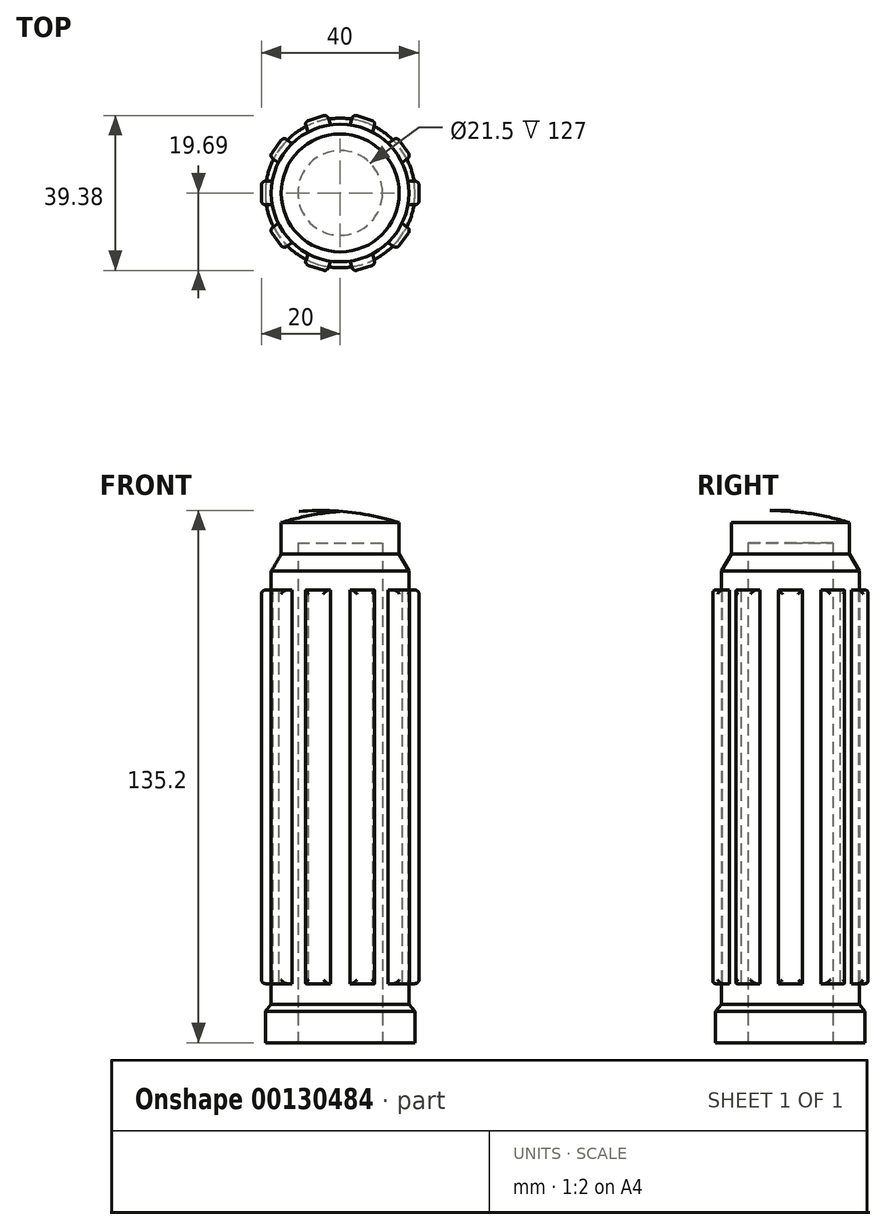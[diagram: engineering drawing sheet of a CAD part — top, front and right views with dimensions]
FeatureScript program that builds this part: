
annotation { "Feature Type Name" : "Feature", "Feature Type Description" : "" }
export const myFeature = defineFeature(function(context is Context, id is Id, definition is map)
    precondition{}
    {
        {
            var Q0;
            Q0=qCreatedBy(makeId("Front.planeOp"),FACE);
            var sketch = newSketch(context, id + "F0", { "sketchPlane" : qUnion([Q0])});
            skLineSegment(sketch, "E0", {"start": v(0, 135) * mm, "end": v(0, 127) * mm});
            skLineSegment(sketch, "E1", {"start": v(0, 127) * mm, "end": v(10.75, 127) * mm});
            skLineSegment(sketch, "E2", {"start": v(10.75, 127) * mm, "end": v(10.75, 0) * mm});
            skLineSegment(sketch, "E3", {"start": v(10.75, 0) * mm, "end": v(19, 0) * mm});
            skLineSegment(sketch, "E4", {"start": v(19, 0) * mm, "end": v(19, 8) * mm});
            skLineSegment(sketch, "E5", {"start": v(19, 8) * mm, "end": v(17.5, 9.79) * mm});
            skLineSegment(sketch, "E6", {"start": v(17.5, 9.79) * mm, "end": v(17.5, 119.79) * mm});
            skLineSegment(sketch, "E7", {"start": v(15, 124.12) * mm, "end": v(15, 132.12) * mm});
            skArc(sketch, "E8", {"start": v(15, 132.12) * mm, "mid": v(7.58, 133.98) * mm, "end": v(0, 135) * mm});
            skLineSegment(sketch, "E9", {"start": v(17.5, 119.79) * mm, "end": v(15, 124.12) * mm});
            skLineSegment(sketch, "E10", {"start": v(0, 0) * mm, "end": v(0, 165.13) * mm, "construction": true});
            skSolve(sketch);
        }
        {
            var Q0;
            Q0=makeQuery(id+"F0.imprint","IMPRINT",FACE,{"disambiguationData":[TD([[makeQuery(id+"F0.imprint","IMPRINT",EDGE,{"derivedFrom":sQuery(id+"F0.wireOp",EDGE,"E0")}),1.0]])]});
            var Q1;
            Q1=sQuery(id+"F0.wireOp",EDGE,"E10");
            revolve(context, id + "F1", {"entities" : qUnion([Q0]), "axis" : qUnion([Q1]), "revolveType" : RevolveType.FULL});
        }
        {
            var Q0;
            Q0=qCreatedBy(makeId("Right.planeOp"),FACE);
            cPlane(context, id + "F2", {"entities" : qUnion([Q0]), "cplaneType" : CPlaneType.OFFSET, "offset" : 20 * mm, "width" : 150 * mm, "height" : 150 * mm});
        }
        {
            var Q0;
            Q0=qCreatedBy(id+"F2.planeOp",FACE);
            var sketch = newSketch(context, id + "F3", { "sketchPlane" : qUnion([Q0])});
            skLineSegment(sketch, "E11.bottom", {"start": v(-3, 115) * mm, "end": v(3, 115) * mm});
            skLineSegment(sketch, "E11.top", {"start": v(-3, 15) * mm, "end": v(3, 15) * mm});
            skLineSegment(sketch, "E11.left", {"start": v(-3, 115) * mm, "end": v(-3, 15) * mm});
            skLineSegment(sketch, "E11.right", {"start": v(3, 115) * mm, "end": v(3, 15) * mm});
            skSolve(sketch);
        }
        {
            var Q0;
            Q0=makeQuery(id+"F3.imprint","IMPRINT",FACE,{"disambiguationData":[TD([[makeQuery(id+"F3.imprint","IMPRINT",EDGE,{"derivedFrom":sQuery(id+"F3.wireOp",EDGE,"E11.bottom")}),-1.0]])]});
            var Q1;
            Q1=makeQuery(id+"F1.opRevolve","SWEPT_FACE",FACE,{"disambiguationData":[OSD([sQuery(id+"F0.wireOp",EDGE,"E6")])]});
            extrude(context, id + "F4", {"entities" : qUnion([Q0]), "endBound" : BoundingType.UP_TO_SURFACE, "oppositeDirection" : true, "endBoundEntityFace" : qUnion([Q1]), "depth" : 25 * mm});
        }
        {
            var Q0;
            Q0=makeQuery(id+"F4.opExtrude","CAP_EDGE",EDGE,{"disambiguationData":[OSD([sQuery(id+"F3.wireOp",EDGE,"E11.right")])],"isStart":true});
            var Q1;
            Q1=makeQuery(id+"F4.opExtrude","CAP_EDGE",EDGE,{"disambiguationData":[OSD([sQuery(id+"F3.wireOp",EDGE,"E11.bottom")])],"isStart":true});
            var Q2;
            Q2=makeQuery(id+"F4.opExtrude","CAP_EDGE",EDGE,{"disambiguationData":[OSD([sQuery(id+"F3.wireOp",EDGE,"E11.top")])],"isStart":true});
            var Q3;
            Q3=makeQuery(id+"F4.opExtrude","CAP_EDGE",EDGE,{"disambiguationData":[OSD([sQuery(id+"F3.wireOp",EDGE,"E11.left")])],"isStart":true});
            fillet(context, id + "F5", {"entities" : qUnion([Q0, Q1, Q2, Q3]), "radius" : 1 * mm, "tangentPropagation" : true, "allowEdgeOverflow" : false});
        }
        {
            var Q0;
            Q0=makeQuery(id+"F4.opExtrude","SWEPT_BODY",BODY,{"disambiguationData":[OSD([sQuery(id+"F3.wireOp",EDGE,"E11.bottom"),sQuery(id+"F3.wireOp",EDGE,"E11.top"),sQuery(id+"F3.wireOp",EDGE,"E11.left"),sQuery(id+"F3.wireOp",EDGE,"E11.right")])]});
            var Q1;
            Q1=sQuery(id+"F0.wireOp",EDGE,"E10");
            circularPattern(context, id + "F6", {"entities" : qUnion([Q0]), "axis" : qUnion([Q1]), "angle" : 360 * degree, "instanceCount" : 10, "equalSpace" : true});
        }
    });
